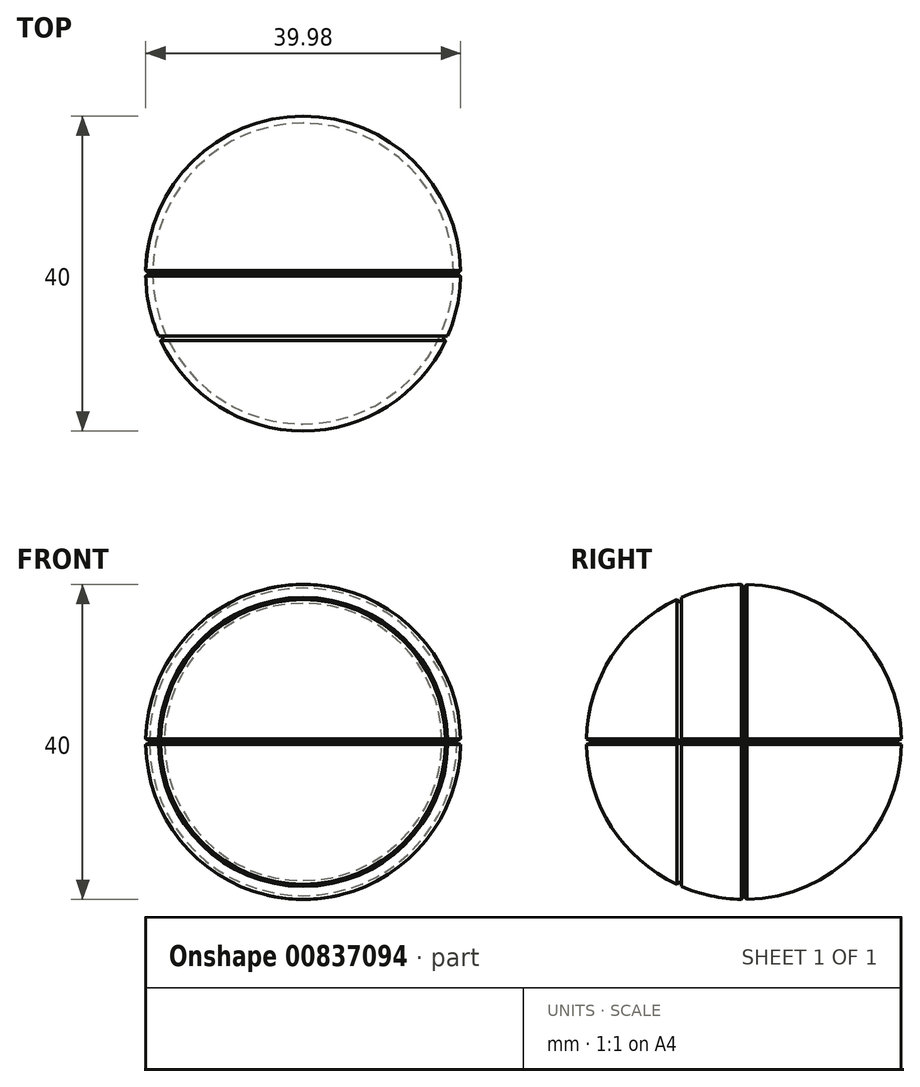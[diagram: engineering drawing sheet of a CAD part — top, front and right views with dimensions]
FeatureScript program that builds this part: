
annotation { "Feature Type Name" : "Feature", "Feature Type Description" : "" }
export const myFeature = defineFeature(function(context is Context, id is Id, definition is map)
    precondition{}
    {
        {
            var Q0;
            Q0=qCreatedBy(makeId("Front.planeOp"),FACE);
            var sketch = newSketch(context, id + "F0", { "sketchPlane" : qUnion([Q0])});
            skCircle(sketch, "E0", {"center": v(0, 0) * mm, "radius": 20 * mm});
            skLineSegment(sketch, "E1", {"start": v(0, 20) * mm, "end": v(0, -20) * mm});
            skSolve(sketch);
        }
        {
            var Q0;
            {var subQ0=sQuery(id+"F0.wireOp",EDGE,"E1");Q0=makeQuery(id+"F0.imprint","IMPRINT",FACE,{"disambiguationData":[TD([[makeQuery(id+"F0.imprint","IMPRINT",EDGE,{"derivedFrom":subQ0}),-1.0]])]});}
            var Q1;
            Q1=sQuery(id+"F0.wireOp",EDGE,"E1");
            revolve(context, id + "F1", {"surfaceOperationType" : NewSurfaceOperationType.NEW, "entities" : qUnion([Q0]), "axis" : qUnion([Q1]), "revolveType" : RevolveType.FULL});
        }
        {
            var Q0;
            Q0=qCreatedBy(makeId("Right.planeOp"),FACE);
            var sketch = newSketch(context, id + "F2", { "sketchPlane" : qUnion([Q0])});
            skLineSegment(sketch, "E2", {"start": v(-7.93, 19.31) * mm, "end": v(-7.93, 17.62) * mm});
            skLineSegment(sketch, "E3", {"start": v(-7.93, 17.62) * mm, "end": v(-9.63, 18.93) * mm});
            skLineSegment(sketch, "E4", {"start": v(-9.63, 18.93) * mm, "end": v(-7.93, 19.31) * mm});
            skLineSegment(sketch, "E5", {"start": v(0, 0) * mm, "end": v(-22.58, 0) * mm});
            skSolve(sketch);
        }
        {
            var Q0;
            Q0=makeQuery(id+"F2.imprint","IMPRINT",FACE,{"disambiguationData":[TD([[makeQuery(id+"F2.imprint","IMPRINT",EDGE,{"derivedFrom":sQuery(id+"F2.wireOp",EDGE,"E2")}),-1.0]])]});
            var Q1;
            Q1=sQuery(id+"F2.wireOp",EDGE,"E5");
            revolve(context, id + "F3", {"operationType" : NewBodyOperationType.REMOVE, "surfaceOperationType" : NewSurfaceOperationType.NEW, "entities" : qUnion([Q0]), "axis" : qUnion([Q1]), "revolveType" : RevolveType.FULL, "oppositeDirection" : true});
        }
        {
            var Q0;
            Q0=qCreatedBy(makeId("Right.planeOp"),FACE);
            var sketch = newSketch(context, id + "F4", { "sketchPlane" : qUnion([Q0])});
            skLineSegment(sketch, "E6", {"start": v(19.1, 0) * mm, "end": v(24.57, 2.26) * mm});
            skLineSegment(sketch, "E7", {"start": v(24.57, 2.26) * mm, "end": v(24.57, 0) * mm});
            skLineSegment(sketch, "E8", {"start": v(21.84, 1.13) * mm, "end": v(24.35, 3.75) * mm});
            skLineSegment(sketch, "E9", {"start": v(19.1, 0) * mm, "end": v(24.58, -1.97) * mm});
            skLineSegment(sketch, "E10", {"start": v(24.58, -1.97) * mm, "end": v(24.57, 0) * mm});
            skLineSegment(sketch, "E11", {"start": v(0, 20.07) * mm, "end": v(0, 0) * mm});
            skSolve(sketch);
        }
        {
            var Q0;
            {var subQ1=sQuery(id+"F4.wireOp",EDGE,"E7");Q0=makeQuery(id+"F4.imprint","IMPRINT",FACE,{"disambiguationData":[TD([[makeQuery(id+"F4.imprint","IMPRINT",EDGE,{"derivedFrom":subQ1}),-1.0]])]});}
            var Q1;
            Q1=sQuery(id+"F4.wireOp",EDGE,"E11");
            revolve(context, id + "F5", {"operationType" : NewBodyOperationType.REMOVE, "surfaceOperationType" : NewSurfaceOperationType.NEW, "entities" : qUnion([Q0]), "axis" : qUnion([Q1]), "revolveType" : RevolveType.FULL, "oppositeDirection" : true});
        }
        {
            var Q0;
            Q0=qCreatedBy(makeId("Right.planeOp"),FACE);
            var sketch = newSketch(context, id + "F6", { "sketchPlane" : qUnion([Q0])});
            skLineSegment(sketch, "E12", {"start": v(1.41, 21.33) * mm, "end": v(0, 19.53) * mm});
            skLineSegment(sketch, "E13", {"start": v(0, 19.53) * mm, "end": v(-1.25, 21.33) * mm});
            skLineSegment(sketch, "E14", {"start": v(-1.25, 21.33) * mm, "end": v(1.41, 21.33) * mm});
            skLineSegment(sketch, "E15", {"start": v(0, 0) * mm, "end": v(-9.82, 0) * mm});
            skSolve(sketch);
        }
        {
            var Q0;
            Q0=makeQuery(id+"F6.imprint","IMPRINT",FACE,{"disambiguationData":[TD([[makeQuery(id+"F6.imprint","IMPRINT",EDGE,{"derivedFrom":sQuery(id+"F6.wireOp",EDGE,"E12")}),-1.0]])]});
            var Q1;
            Q1=sQuery(id+"F6.wireOp",EDGE,"E15");
            revolve(context, id + "F7", {"operationType" : NewBodyOperationType.REMOVE, "surfaceOperationType" : NewSurfaceOperationType.NEW, "entities" : qUnion([Q0]), "axis" : qUnion([Q1]), "revolveType" : RevolveType.FULL});
        }
    });
